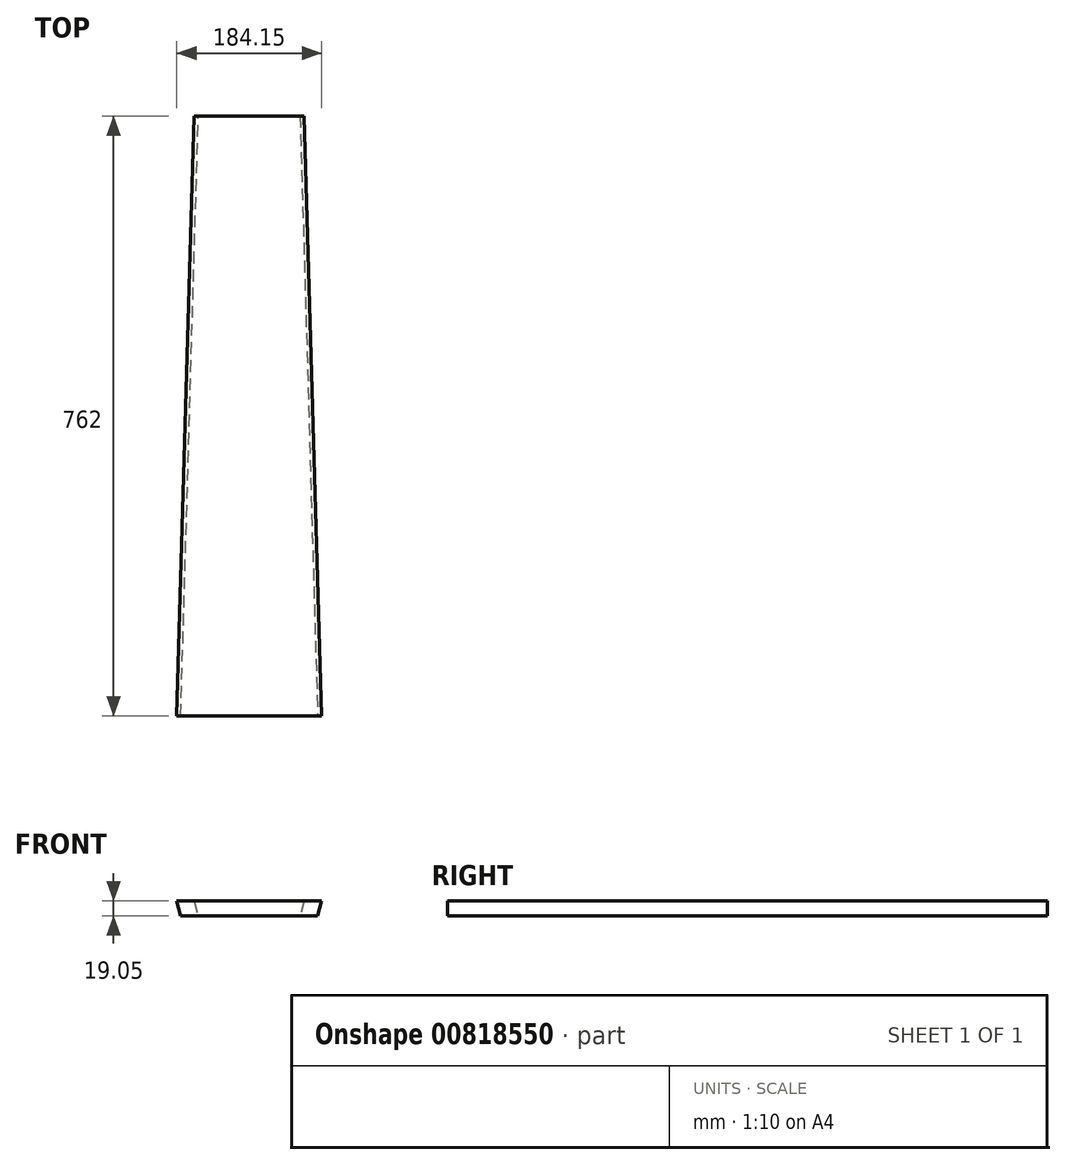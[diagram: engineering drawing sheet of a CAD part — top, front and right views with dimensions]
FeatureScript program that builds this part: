
annotation { "Feature Type Name" : "Feature", "Feature Type Description" : "" }
export const myFeature = defineFeature(function(context is Context, id is Id, definition is map)
    precondition{}
    {
        {
            var Q0;
            Q0=qCreatedBy(makeId("Top.planeOp"),FACE);
            var sketch = newSketch(context, id + "F0", { "sketchPlane" : qUnion([Q0])});
            skLineSegment(sketch, "E0", {"start": v(0, 0) * mm, "end": v(184.15, 0) * mm});
            skLineSegment(sketch, "E1", {"start": v(184.15, 0) * mm, "end": v(161.92, 762) * mm});
            skLineSegment(sketch, "E2", {"start": v(161.92, 762) * mm, "end": v(22.22, 762) * mm});
            skLineSegment(sketch, "E3", {"start": v(22.22, 762) * mm, "end": v(0, 0) * mm});
            skSolve(sketch);
        }
        {
            var Q0;
            Q0=makeQuery(id+"F0.imprint","IMPRINT",FACE,{"disambiguationData":[TD([[makeQuery(id+"F0.imprint","IMPRINT",EDGE,{"derivedFrom":sQuery(id+"F0.wireOp",EDGE,"E0")}),1.0]])]});
            extrude(context, id + "F1", {"entities" : qUnion([Q0]), "depth" : 19.05 * mm, "offsetDistance" : 25.4 * mm});
        }
        {
            var Q0;
            Q0=makeQuery(id+"F1.opExtrude","SWEPT_FACE",FACE,{"disambiguationData":[OSD([sQuery(id+"F0.wireOp",EDGE,"E2")])]});
            var sketch = newSketch(context, id + "F2", { "sketchPlane" : qUnion([Q0])});
            skLineSegment(sketch, "E4", {"start": v(-161.92, 19.05) * mm, "end": v(-156.82, 0) * mm});
            skLineSegment(sketch, "E5.0", {"start": v(-161.92, 19.05) * mm, "end": v(-161.92, 0) * mm});
            skLineSegment(sketch, "E5.1", {"start": v(-161.92, 0) * mm, "end": v(-156.82, 0) * mm});
            skPoint(sketch, "E6.orphan", {"position": v(-22.22, 0) * mm});
            skSolve(sketch);
        }
        {
            var Q0;
            Q0=makeQuery(id+"F1.opExtrude","SWEPT_FACE",FACE,{"disambiguationData":[OSD([sQuery(id+"F0.wireOp",EDGE,"E0")])]});
            var sketch = newSketch(context, id + "F3", { "sketchPlane" : qUnion([Q0])});
            skLineSegment(sketch, "E7.0", {"start": v(184.15, 19.05) * mm, "end": v(184.15, 0) * mm});
            skLineSegment(sketch, "E8.0", {"start": v(179.05, 0) * mm, "end": v(184.15, 0) * mm});
            skLineSegment(sketch, "E9", {"start": v(184.15, 19.05) * mm, "end": v(179.05, 0) * mm});
            skPoint(sketch, "E10.orphan", {"position": v(0, 0) * mm});
            skSolve(sketch);
        }
        {
            var Q1;
            Q1 = qSketchRegion(id + "F2", true);
            var Q2;
            Q2 = qSketchRegion(id + "F3", true);
            var Q3;
            Q3=makeQuery(id+"F1.opExtrude","CAP_EDGE",EDGE,{"disambiguationData":[OSD([sQuery(id+"F0.wireOp",EDGE,"E1")])],"isStart":false});
            loft(context, id + "F4", {"operationType" : NewBodyOperationType.REMOVE, "addGuides" : true, "sheetProfilesArray" : [{ "sheetProfileEntities" : qUnion([Q1]) }, { "sheetProfileEntities" : qUnion([Q2]) }], "guidesArray" : [{ "guideEntities" : qUnion([Q3]), "guideDerivativeType" : LoftGuideDerivativeType.DEFAULT, "guideDerivativeMagnitude" : 1 }]});
        }
        {
            var Q0;
            Q0=makeQuery(id+"F1.opExtrude","SWEPT_FACE",FACE,{"disambiguationData":[OSD([sQuery(id+"F0.wireOp",EDGE,"E0")])]});
            var sketch = newSketch(context, id + "F5", { "sketchPlane" : qUnion([Q0])});
            skLineSegment(sketch, "E11.0", {"start": v(0, 0) * mm, "end": v(5.1, 0) * mm});
            skLineSegment(sketch, "E12.0", {"start": v(0, 19.05) * mm, "end": v(0, 0) * mm});
            skLineSegment(sketch, "E13", {"start": v(0, 19.05) * mm, "end": v(5.1, 0) * mm});
            skPoint(sketch, "E14.orphan", {"position": v(179.05, 0) * mm});
            skSolve(sketch);
        }
        {
            var Q0;
            Q0=makeQuery(id+"F1.opExtrude","SWEPT_FACE",FACE,{"disambiguationData":[OSD([sQuery(id+"F0.wireOp",EDGE,"E2")])]});
            var sketch = newSketch(context, id + "F6", { "sketchPlane" : qUnion([Q0])});
            skLineSegment(sketch, "E15", {"start": v(-22.22, 19.05) * mm, "end": v(-27.33, 0) * mm});
            skLineSegment(sketch, "E16.0", {"start": v(-22.22, 19.05) * mm, "end": v(-22.22, 0) * mm});
            skLineSegment(sketch, "E17.0", {"start": v(-27.33, 0) * mm, "end": v(-22.22, 0) * mm});
            skPoint(sketch, "E18.orphan", {"position": v(-156.82, 0) * mm});
            skSolve(sketch);
        }
        {
            var Q1;
            Q1 = qSketchRegion(id + "F5", true);
            var Q2;
            Q2 = qSketchRegion(id + "F6", true);
            var Q3;
            Q3=makeQuery(id+"F1.opExtrude","CAP_EDGE",EDGE,{"disambiguationData":[OSD([sQuery(id+"F0.wireOp",EDGE,"E3")])],"isStart":false});
            loft(context, id + "F7", {"operationType" : NewBodyOperationType.REMOVE, "addGuides" : true, "sheetProfilesArray" : [{ "sheetProfileEntities" : qUnion([Q1]) }, { "sheetProfileEntities" : qUnion([Q2]) }], "guidesArray" : [{ "guideEntities" : qUnion([Q3]), "guideDerivativeType" : LoftGuideDerivativeType.DEFAULT, "guideDerivativeMagnitude" : 1 }]});
        }
    });
